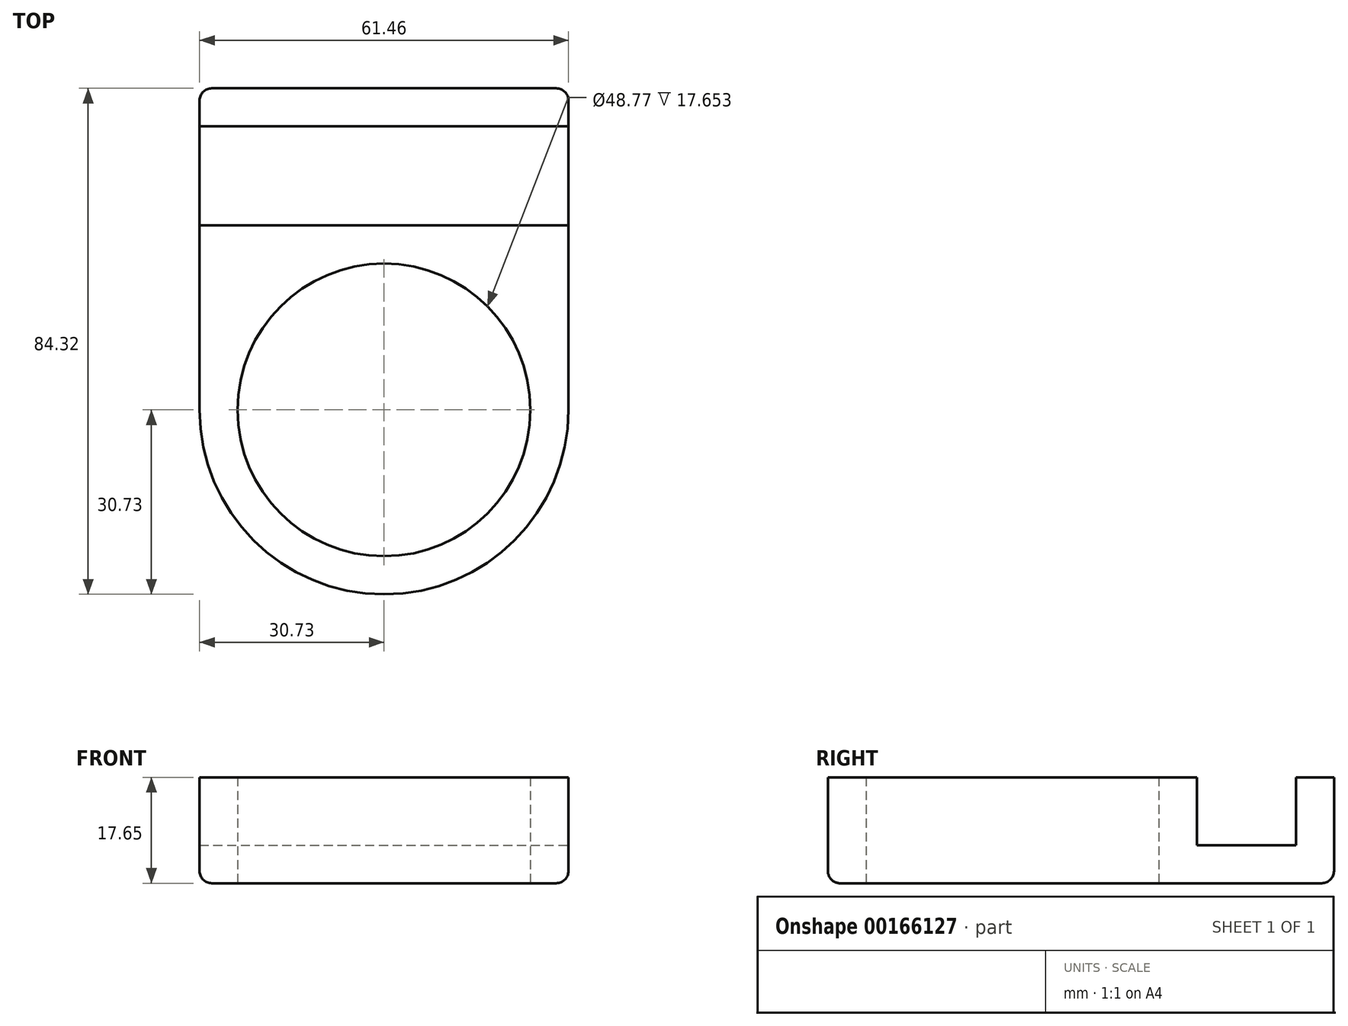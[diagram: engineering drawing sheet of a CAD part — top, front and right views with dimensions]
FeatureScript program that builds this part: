
annotation { "Feature Type Name" : "Feature", "Feature Type Description" : "" }
export const myFeature = defineFeature(function(context is Context, id is Id, definition is map)
    precondition{}
    {
        {
            var Q0;
            Q0=qCreatedBy(makeId("Top.planeOp"),FACE);
            var sketch = newSketch(context, id + "F0", { "sketchPlane" : qUnion([Q0])});
            skCircle(sketch, "E0", {"center": v(0, 0) * mm, "radius": 24.38 * mm});
            skLineSegment(sketch, "E1", {"start": v(-30.73, 0) * mm, "end": v(-30.73, 53.6) * mm});
            skLineSegment(sketch, "E2", {"start": v(-30.73, 53.6) * mm, "end": v(30.73, 53.6) * mm});
            skLineSegment(sketch, "E3", {"start": v(30.73, 53.6) * mm, "end": v(30.73, 0) * mm});
            skArc(sketch, "E4", {"start": v(-30.73, 0) * mm, "mid": v(0, -30.73) * mm, "end": v(30.73, 0) * mm});
            skPoint(sketch, "E5", {"position": v(0, 53.6) * mm});
            skLineSegment(sketch, "E6", {"start": v(-30.73, 0) * mm, "end": v(-24.38, 0) * mm, "construction": true});
            skLineSegment(sketch, "E7", {"start": v(0, 53.6) * mm, "end": v(0, 24.38) * mm, "construction": true});
            skSolve(sketch);
        }
        {
            var Q0;
            Q0 = qSketchRegion(id + "F0", true);
            extrude(context, id + "F1", {"entities" : qUnion([Q0]), "depth" : 6.35 * mm});
        }
        {
            var Q0;
            Q0=makeQuery(id+"F1.opExtrude","CAP_FACE",FACE,{"disambiguationData":[OSD([sQuery(id+"F0.wireOp",EDGE,"E0"),sQuery(id+"F0.wireOp",EDGE,"E1"),sQuery(id+"F0.wireOp",EDGE,"E2"),sQuery(id+"F0.wireOp",EDGE,"E3"),sQuery(id+"F0.wireOp",EDGE,"E4")])],"isStart":false});
            var sketch = newSketch(context, id + "F2", { "sketchPlane" : qUnion([Q0])});
            skLineSegment(sketch, "E8.bottom", {"start": v(-30.73, 53.6) * mm, "end": v(30.73, 53.6) * mm});
            skLineSegment(sketch, "E8.top", {"start": v(-30.73, 47.24) * mm, "end": v(30.73, 47.24) * mm});
            skLineSegment(sketch, "E8.left", {"start": v(-30.73, 53.6) * mm, "end": v(-30.73, 47.24) * mm});
            skLineSegment(sketch, "E8.right", {"start": v(30.73, 53.6) * mm, "end": v(30.73, 47.24) * mm});
            skLineSegment(sketch, "E9", {"start": v(-30.73, 30.73) * mm, "end": v(-30.73, 0) * mm});
            skLineSegment(sketch, "E10", {"start": v(-30.73, 30.73) * mm, "end": v(30.73, 30.73) * mm});
            skLineSegment(sketch, "E11", {"start": v(30.73, 30.73) * mm, "end": v(30.73, 0) * mm});
            skArc(sketch, "E12", {"start": v(-30.73, 0) * mm, "mid": v(0, -30.73) * mm, "end": v(30.73, 0) * mm});
            skLineSegment(sketch, "E13", {"start": v(0, 24.38) * mm, "end": v(0, 30.73) * mm, "construction": true});
            skCircle(sketch, "E14", {"center": v(0, 0) * mm, "radius": 24.38 * mm});
            skSolve(sketch);
        }
        {
            var Q0;
            Q0 = qSketchRegion(id + "F2", true);
            extrude(context, id + "F3", {"entities" : qUnion([Q0]), "operationType" : NewBodyOperationType.ADD, "depth" : 11.3 * mm});
        }
        {
            var Q0;
            Q0=makeQuery(id+"F1.opExtrude","CAP_EDGE",EDGE,{"disambiguationData":[OSD([sQuery(id+"F0.wireOp",EDGE,"E4")])],"isStart":true});
            var Q1;
            Q1=makeQuery(id+"F1.opExtrude","CAP_EDGE",EDGE,{"disambiguationData":[OSD([sQuery(id+"F0.wireOp",EDGE,"E2")])],"isStart":true});
            var Q2;
            Q2=makeQuery(id+"F3.boolean.opBoolean","MERGE",EDGE,{"derivedFrom":[makeQuery(id+"F1.opExtrude","SWEPT_EDGE",EDGE,{"disambiguationData":[OSD([sQuery(id+"F0.wireOp",EDGE,"E2"),sQuery(id+"F0.wireOp",EDGE,"E3")])]}),makeQuery(id+"F3.opExtrude","SWEPT_EDGE",EDGE,{"disambiguationData":[OSD([sQuery(id+"F2.wireOp",EDGE,"E8.bottom"),sQuery(id+"F2.wireOp",EDGE,"E8.right")])]})]});
            var Q3;
            Q3=makeQuery(id+"F3.boolean.opBoolean","MERGE",EDGE,{"derivedFrom":[makeQuery(id+"F1.opExtrude","SWEPT_EDGE",EDGE,{"disambiguationData":[OSD([sQuery(id+"F0.wireOp",EDGE,"E1"),sQuery(id+"F0.wireOp",EDGE,"E2")])]}),makeQuery(id+"F3.opExtrude","SWEPT_EDGE",EDGE,{"disambiguationData":[OSD([sQuery(id+"F2.wireOp",EDGE,"E8.bottom"),sQuery(id+"F2.wireOp",EDGE,"E8.left")])]})]});
            fillet(context, id + "F4", {"entities" : qUnion([Q0, Q1, Q2, Q3]), "radius" : 2.03 * mm, "tangentPropagation" : true, "allowEdgeOverflow" : false});
        }
    });
